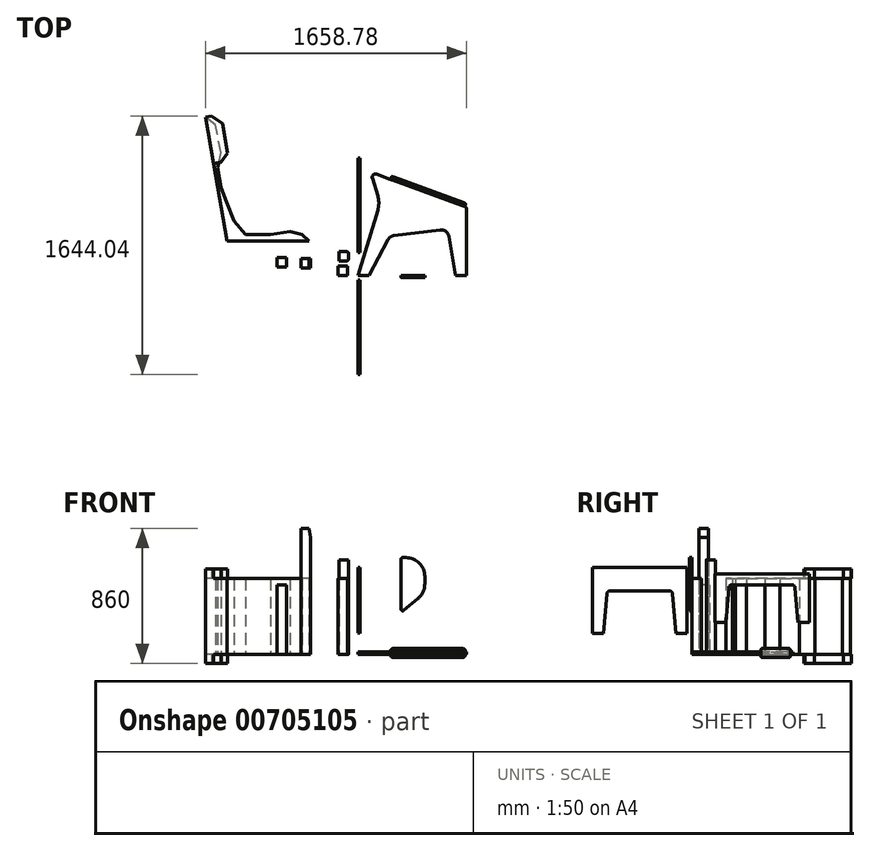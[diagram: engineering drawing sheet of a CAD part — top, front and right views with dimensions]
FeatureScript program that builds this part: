
annotation { "Feature Type Name" : "Feature", "Feature Type Description" : "" }
export const myFeature = defineFeature(function(context is Context, id is Id, definition is map)
    precondition{}
    {
        {
            var Q0;
            Q0=qCreatedBy(makeId("Top.planeOp"),FACE);
            var sketch = newSketch(context, id + "F0", { "sketchPlane" : qUnion([Q0])});
            skLineSegment(sketch, "E0.bottom", {"start": v(0, 0) * mm, "end": v(70, 0) * mm});
            skLineSegment(sketch, "E0.right", {"start": v(690, 0) * mm, "end": v(690, 420) * mm});
            skLineSegment(sketch, "E1", {"start": v(117.7, 642.3) * mm, "end": v(676.84, 438.8) * mm});
            skLineSegment(sketch, "E2", {"start": v(126.56, 503.75) * mm, "end": v(91.73, 617.66) * mm});
            skLineSegment(sketch, "E3", {"start": v(70, 0) * mm, "end": v(191.89, 227.17) * mm});
            skLineSegment(sketch, "E4", {"start": v(229.85, 253.16) * mm, "end": v(523.12, 289.17) * mm});
            skLineSegment(sketch, "E5", {"start": v(578.53, 247.8) * mm, "end": v(620, 0) * mm});
            skLineSegment(sketch, "E6", {"start": v(0, 0) * mm, "end": v(126.62, 416.24) * mm});
            skPoint(sketch, "E7.visualSharp", {"position": v(570.63, 295) * mm});
            skArc(sketch, "E7.filletArc", {"start": v(578.53, 247.8) * mm, "mid": v(559.13, 279.6) * mm, "end": v(523.12, 289.17) * mm});
            skPoint(sketch, "E8.visualSharp", {"position": v(204.13, 250) * mm});
            skArc(sketch, "E8.filletArc", {"start": v(229.85, 253.16) * mm, "mid": v(207.7, 244.79) * mm, "end": v(191.89, 227.17) * mm});
            skPoint(sketch, "E9.visualSharp", {"position": v(139.93, 460) * mm});
            skArc(sketch, "E9.filletArc", {"start": v(126.62, 416.24) * mm, "mid": v(133.11, 460) * mm, "end": v(126.56, 503.75) * mm});
            skArc(sketch, "E10.filletArc", {"start": v(690, 420) * mm, "mid": v(686.38, 431.47) * mm, "end": v(676.84, 438.8) * mm});
            skLineSegment(sketch, "E11.trimOffspring", {"start": v(620, 0) * mm, "end": v(690, 0) * mm});
            skPoint(sketch, "E12.visualSharp", {"position": v(80, 656.03) * mm});
            skArc(sketch, "E12.filletArc", {"start": v(117.7, 642.3) * mm, "mid": v(97.09, 638.02) * mm, "end": v(91.73, 617.66) * mm});
            skSolve(sketch);
        }
        {
            var Q0;
            Q0=makeQuery(id+"F0.imprint","IMPRINT",FACE,{"disambiguationData":[TD([[makeQuery(id+"F0.imprint","IMPRINT",EDGE,{"derivedFrom":sQuery(id+"F0.wireOp",EDGE,"E0.bottom")}),1.0]])]});
            extrude(context, id + "F1", {"entities" : qUnion([Q0]), "depth" : 15 * mm, "offsetDistance" : 25 * mm});
        }
        {
            var Q0;
            Q0=makeQuery(id+"F1.opExtrude","SWEPT_FACE",FACE,{"disambiguationData":[OSD([sQuery(id+"F0.wireOp",EDGE,"E1")])]});
            var sketch = newSketch(context, id + "F2", { "sketchPlane" : qUnion([Q0])});
            skLineSegment(sketch, "E13.bottom", {"start": v(-470.95, 35) * mm, "end": v(-0.95, 35) * mm});
            skLineSegment(sketch, "E13.top", {"start": v(-470.95, -20) * mm, "end": v(-0.95, -20) * mm});
            skLineSegment(sketch, "E13.left", {"start": v(-485.95, 20) * mm, "end": v(-485.95, -5) * mm});
            skLineSegment(sketch, "E13.right", {"start": v(14.05, 20) * mm, "end": v(14.05, -5) * mm});
            skPoint(sketch, "E14.visualSharp", {"position": v(-485.95, 35) * mm});
            skArc(sketch, "E14.filletArc", {"start": v(-470.95, 35) * mm, "mid": v(-481.55, 30.6) * mm, "end": v(-485.95, 20) * mm});
            skPoint(sketch, "E15.visualSharp", {"position": v(-485.95, -20) * mm});
            skArc(sketch, "E15.filletArc", {"start": v(-485.95, -5) * mm, "mid": v(-481.55, -15.6) * mm, "end": v(-470.95, -20) * mm});
            skPoint(sketch, "E16.visualSharp", {"position": v(14.05, 35) * mm});
            skArc(sketch, "E16.filletArc", {"start": v(14.05, 20) * mm, "mid": v(9.66, 30.6) * mm, "end": v(-0.95, 35) * mm});
            skPoint(sketch, "E17.visualSharp", {"position": v(14.05, -20) * mm});
            skArc(sketch, "E17.filletArc", {"start": v(-0.95, -20) * mm, "mid": v(9.66, -15.6) * mm, "end": v(14.05, -5) * mm});
            skSolve(sketch);
        }
        {
            var Q0;
            Q0 = qSketchRegion(id + "F2", true);
            extrude(context, id + "F3", {"entities" : qUnion([Q0]), "operationType" : NewBodyOperationType.ADD, "depth" : 20 * mm, "offsetDistance" : 25 * mm});
        }
        {
            var Q0;
            Q0=makeQuery(id+"F3.opExtrude","CAP_EDGE",EDGE,{"disambiguationData":[OSD([sQuery(id+"F2.wireOp",EDGE,"E13.top")])],"isStart":false});
            fillet(context, id + "F4", {"entities" : qUnion([Q0]), "radius" : 5 * mm, "tangentPropagation" : true, "allowEdgeOverflow" : false});
        }
        {
            var Q0;
            Q0=qCreatedBy(makeId("Front.planeOp"),FACE);
            var sketch = newSketch(context, id + "F5", { "sketchPlane" : qUnion([Q0])});
            skLineSegment(sketch, "E18.top", {"start": v(0, -1013.8) * mm, "end": v(626.68, -1013.8) * mm});
            skLineSegment(sketch, "E18.left", {"start": v(-123.43, -313.8) * mm, "end": v(0, -1013.8) * mm});
            skLineSegment(sketch, "E18.right", {"start": v(640.31, -922.17) * mm, "end": v(651.3, -984.47) * mm});
            skLineSegment(sketch, "E19", {"start": v(538.32, -839.6) * mm, "end": v(134.26, -853.8) * mm});
            skPoint(sketch, "E20.visualSharp", {"position": v(625.21, -836.54) * mm});
            skArc(sketch, "E20.filletArc", {"start": v(640.31, -922.17) * mm, "mid": v(604.75, -861.81) * mm, "end": v(538.32, -839.6) * mm});
            skPoint(sketch, "E21.visualSharp", {"position": v(656.47, -1013.8) * mm});
            skArc(sketch, "E21.filletArc", {"start": v(626.68, -1013.8) * mm, "mid": v(645.83, -1004.88) * mm, "end": v(651.3, -984.47) * mm});
            skLineSegment(sketch, "E22", {"start": v(39.04, -313.8) * mm, "end": v(134.26, -853.8) * mm});
            skLineSegment(sketch, "E23.top", {"start": v(-123.43, -13.8) * mm, "end": v(39.04, -13.8) * mm});
            skLineSegment(sketch, "E23.left", {"start": v(-123.43, -313.8) * mm, "end": v(-123.43, -13.8) * mm});
            skLineSegment(sketch, "E23.right", {"start": v(39.04, -313.8) * mm, "end": v(39.04, -13.8) * mm});
            skPoint(sketch, "E24.visualSharp", {"position": v(39.04, -13.8) * mm});
            skSolve(sketch);
        }
        {
            var Q0;
            Q0 = qSketchRegion(id + "F5", true);
            extrude(context, id + "F6", {"entities" : qUnion([Q0]), "depth" : 600 * mm, "offsetDistance" : 25 * mm});
        }
        {
            var Q0;
            Q0=makeQuery(id+"F6.opExtrude","SWEPT_EDGE",EDGE,{"disambiguationData":[OSD([sQuery(id+"F5.wireOp",EDGE,"E18.top"),sQuery(id+"F5.wireOp",EDGE,"E18.left")])]});
            fillet(context, id + "F7", {"entities" : qUnion([Q0]), "radius" : 50 * mm, "tangentPropagation" : true, "allowEdgeOverflow" : false});
        }
        {
            var Q0;
            Q0=makeQuery(id+"F6.opExtrude","SWEPT_FACE",FACE,{"disambiguationData":[OSD([sQuery(id+"F5.wireOp",EDGE,"E23.top")])]});
            var sketch = newSketch(context, id + "F8", { "sketchPlane" : qUnion([Q0])});
            skLineSegment(sketch, "E25", {"start": v(39.04, -600) * mm, "end": v(-123.43, -600) * mm});
            skLineSegment(sketch, "E26", {"start": v(-123.43, -600) * mm, "end": v(66.57, -689.38) * mm});
            skLineSegment(sketch, "E27", {"start": v(66.57, -689.38) * mm, "end": v(176, -689.38) * mm});
            skLineSegment(sketch, "E28", {"start": v(176, -689.38) * mm, "end": v(39.04, -600) * mm});
            skLineSegment(sketch, "E29", {"start": v(-123.43, -300) * mm, "end": v(-54.44, -300) * mm});
            skLineSegment(sketch, "E30.MirrorCS", {"start": v(-123.43, 0) * mm, "end": v(66.57, 89.38) * mm});
            skLineSegment(sketch, "E31.MirrorCS", {"start": v(39.04, 0) * mm, "end": v(-123.43, 0) * mm});
            skLineSegment(sketch, "E32.MirrorCS", {"start": v(176, 89.38) * mm, "end": v(39.04, 0) * mm});
            skLineSegment(sketch, "E33.MirrorCS", {"start": v(66.57, 89.38) * mm, "end": v(176, 89.38) * mm});
            skSolve(sketch);
        }
        {
            var Q0;
            Q0=makeQuery(id+"F8.imprint","IMPRINT",FACE,{"disambiguationData":[TD([[makeQuery(id+"F8.imprint","IMPRINT",EDGE,{"derivedFrom":sQuery(id+"F8.wireOp",EDGE,"E30.MirrorCS")}),-1.0]])]});
            var Q1;
            Q1=makeQuery(id+"F8.imprint","IMPRINT",FACE,{"disambiguationData":[TD([[makeQuery(id+"F8.imprint","IMPRINT",EDGE,{"derivedFrom":sQuery(id+"F8.wireOp",EDGE,"E25")}),-1.0]])]});
            extrude(context, id + "F9", {"entities" : qUnion([Q0, Q1]), "operationType" : NewBodyOperationType.ADD, "oppositeDirection" : true, "depth" : 300 * mm, "offsetDistance" : 25 * mm});
        }
        {
            var Q0;
            Q0=makeQuery(id+"F9.opExtrude","SWEPT_EDGE",EDGE,{"disambiguationData":[OSD([sQuery(id+"F8.wireOp",EDGE,"E27"),sQuery(id+"F8.wireOp",EDGE,"E28")])]});
            var Q1;
            Q1=makeQuery(id+"F9.opExtrude","SWEPT_EDGE",EDGE,{"disambiguationData":[OSD([sQuery(id+"F8.wireOp",EDGE,"E32.MirrorCS"),sQuery(id+"F8.wireOp",EDGE,"E33.MirrorCS")])]});
            var Q2;
            Q2=makeQuery(id+"F9.opExtrude","SWEPT_EDGE",EDGE,{"disambiguationData":[OSD([sQuery(id+"F8.wireOp",EDGE,"E26"),sQuery(id+"F8.wireOp",EDGE,"E27")])]});
            var Q3;
            {var subQ0=sQuery(id+"F5.wireOp",EDGE,"E23.left");Q3=makeQuery(id+"F9.boolean.opBoolean","MERGE",EDGE,{"derivedFrom":[makeQuery(id+"F6.opExtrude","CAP_EDGE",EDGE,{"disambiguationData":[OSD([subQ0])],"isStart":false}),makeQuery(id+"F9.opExtrude","SWEPT_EDGE",EDGE,{"disambiguationData":[OSD([sQuery(id+"F5.wireOp",EDGE,"E23.top"),subQ0,sQuery(id+"F8.wireOp",EDGE,"E25"),sQuery(id+"F8.wireOp",EDGE,"E26")])]})]});}
            var Q4;
            Q4=makeQuery(id+"F9.opExtrude","SWEPT_EDGE",EDGE,{"disambiguationData":[OSD([sQuery(id+"F8.wireOp",EDGE,"E30.MirrorCS"),sQuery(id+"F8.wireOp",EDGE,"E33.MirrorCS")])]});
            var Q5;
            {var subQ0=sQuery(id+"F5.wireOp",EDGE,"E23.left");Q5=makeQuery(id+"F9.boolean.opBoolean","MERGE",EDGE,{"derivedFrom":[makeQuery(id+"F6.opExtrude","CAP_EDGE",EDGE,{"disambiguationData":[OSD([subQ0])],"isStart":true}),makeQuery(id+"F9.opExtrude","SWEPT_EDGE",EDGE,{"disambiguationData":[OSD([sQuery(id+"F5.wireOp",EDGE,"E23.top"),subQ0,sQuery(id+"F8.wireOp",EDGE,"E30.MirrorCS"),sQuery(id+"F8.wireOp",EDGE,"E31.MirrorCS")])]})]});}
            var Q6;
            {var subQ0=sQuery(id+"F5.wireOp",EDGE,"E23.right");Q6=makeQuery(id+"F9.boolean.opBoolean","MERGE",EDGE,{"derivedFrom":[makeQuery(id+"F6.opExtrude","CAP_EDGE",EDGE,{"disambiguationData":[OSD([subQ0])],"isStart":false}),makeQuery(id+"F9.opExtrude","SWEPT_EDGE",EDGE,{"disambiguationData":[OSD([sQuery(id+"F5.wireOp",EDGE,"E23.top"),subQ0,sQuery(id+"F8.wireOp",EDGE,"E25"),sQuery(id+"F8.wireOp",EDGE,"E28")])]})]});}
            var Q7;
            {var subQ0=sQuery(id+"F5.wireOp",EDGE,"E23.right");Q7=makeQuery(id+"F9.boolean.opBoolean","MERGE",EDGE,{"derivedFrom":[makeQuery(id+"F6.opExtrude","CAP_EDGE",EDGE,{"disambiguationData":[OSD([subQ0])],"isStart":true}),makeQuery(id+"F9.opExtrude","SWEPT_EDGE",EDGE,{"disambiguationData":[OSD([sQuery(id+"F5.wireOp",EDGE,"E23.top"),subQ0,sQuery(id+"F8.wireOp",EDGE,"E31.MirrorCS"),sQuery(id+"F8.wireOp",EDGE,"E32.MirrorCS")])]})]});}
            fillet(context, id + "F10", {"entities" : qUnion([Q0, Q1, Q2, Q3, Q4, Q5, Q6, Q7]), "radius" : 10 * mm, "tangentPropagation" : true, "allowEdgeOverflow" : false});
        }
        {
            var Q0;
            Q0=qCreatedBy(makeId("Right.planeOp"),FACE);
            var sketch = newSketch(context, id + "F11", { "sketchPlane" : qUnion([Q0])});
            skLineSegment(sketch, "E34.bottom", {"start": v(-630.89, 552.12) * mm, "end": v(-30.89, 552.12) * mm});
            skLineSegment(sketch, "E34.top", {"start": v(-630.89, 132.12) * mm, "end": v(-560.89, 132.12) * mm});
            skLineSegment(sketch, "E34.left", {"start": v(-630.89, 552.12) * mm, "end": v(-630.89, 132.12) * mm});
            skLineSegment(sketch, "E34.right", {"start": v(-30.89, 552.12) * mm, "end": v(-30.89, 132.12) * mm});
            skLineSegment(sketch, "E35.bottom", {"start": v(145.52, 510.33) * mm, "end": v(745.52, 510.33) * mm});
            skLineSegment(sketch, "E35.top", {"start": v(145.52, 200.33) * mm, "end": v(215.52, 200.33) * mm});
            skLineSegment(sketch, "E35.left", {"start": v(145.52, 510.33) * mm, "end": v(145.52, 200.33) * mm});
            skLineSegment(sketch, "E35.right", {"start": v(745.52, 510.33) * mm, "end": v(745.52, 200.33) * mm});
            skLineSegment(sketch, "E36", {"start": v(-560.89, 132.12) * mm, "end": v(-538.86, 383.87) * mm});
            skLineSegment(sketch, "E37", {"start": v(-518.94, 402.12) * mm, "end": v(-142.83, 402.12) * mm});
            skLineSegment(sketch, "E38", {"start": v(-122.91, 383.87) * mm, "end": v(-100.89, 132.12) * mm});
            skLineSegment(sketch, "E39", {"start": v(215.52, 200.33) * mm, "end": v(234.92, 422.07) * mm});
            skLineSegment(sketch, "E40", {"start": v(254.85, 440.33) * mm, "end": v(636.2, 440.33) * mm});
            skLineSegment(sketch, "E41", {"start": v(656.12, 422.07) * mm, "end": v(675.52, 200.33) * mm});
            skLineSegment(sketch, "E42.trimOffspring", {"start": v(675.52, 200.33) * mm, "end": v(745.52, 200.33) * mm});
            skPoint(sketch, "E43.visualSharp", {"position": v(236.52, 440.33) * mm});
            skArc(sketch, "E43.filletArc", {"start": v(254.85, 440.33) * mm, "mid": v(241.34, 435.07) * mm, "end": v(234.92, 422.07) * mm});
            skPoint(sketch, "E44.visualSharp", {"position": v(654.53, 440.33) * mm});
            skArc(sketch, "E44.filletArc", {"start": v(656.12, 422.07) * mm, "mid": v(649.71, 435.07) * mm, "end": v(636.2, 440.33) * mm});
            skLineSegment(sketch, "E45.trimOffspring", {"start": v(-100.89, 132.12) * mm, "end": v(-30.89, 132.12) * mm});
            skPoint(sketch, "E46.visualSharp", {"position": v(-537.26, 402.12) * mm});
            skArc(sketch, "E46.filletArc", {"start": v(-518.94, 402.12) * mm, "mid": v(-532.45, 396.87) * mm, "end": v(-538.86, 383.87) * mm});
            skPoint(sketch, "E47.visualSharp", {"position": v(-124.5, 402.12) * mm});
            skArc(sketch, "E47.filletArc", {"start": v(-122.91, 383.87) * mm, "mid": v(-129.32, 396.87) * mm, "end": v(-142.83, 402.12) * mm});
            skSolve(sketch);
        }
        {
            var Q0;
            Q0=makeQuery(id+"F11.imprint","IMPRINT",FACE,{"disambiguationData":[TD([[makeQuery(id+"F11.imprint","IMPRINT",EDGE,{"derivedFrom":sQuery(id+"F11.wireOp",EDGE,"E34.bottom")}),-1.0]])]});
            var Q1;
            Q1=makeQuery(id+"F11.imprint","IMPRINT",FACE,{"disambiguationData":[TD([[makeQuery(id+"F11.imprint","IMPRINT",EDGE,{"derivedFrom":sQuery(id+"F11.wireOp",EDGE,"E35.bottom")}),-1.0]])]});
            extrude(context, id + "F12", {"entities" : qUnion([Q0, Q1]), "depth" : 15 * mm, "offsetDistance" : 25 * mm});
        }
        {
            var Q0;
            Q0=makeQuery(id+"F12.opExtrude","CAP_EDGE",EDGE,{"disambiguationData":[OSD([sQuery(id+"F11.wireOp",EDGE,"E34.top")])],"isStart":true});
            var Q1;
            Q1=makeQuery(id+"F12.opExtrude","CAP_EDGE",EDGE,{"disambiguationData":[OSD([sQuery(id+"F11.wireOp",EDGE,"E45.trimOffspring")])],"isStart":true});
            chamfer(context, id + "F13", {"entities" : qUnion([Q0, Q1]), "chamferType" : ChamferType.OFFSET_ANGLE, "width" : 15 * mm, "oppositeDirection" : false, "angle" : 15 * degree, "tangentPropagation" : true});
        }
        {
            var Q0;
            Q0=makeQuery(id+"F6.opExtrude","SWEPT_BODY",BODY,{"disambiguationData":[OSD([sQuery(id+"F5.wireOp",EDGE,"E18.top"),sQuery(id+"F5.wireOp",EDGE,"E18.left"),sQuery(id+"F5.wireOp",EDGE,"E18.right"),sQuery(id+"F5.wireOp",EDGE,"E19"),sQuery(id+"F5.wireOp",EDGE,"E20.filletArc"),sQuery(id+"F5.wireOp",EDGE,"E21.filletArc"),sQuery(id+"F5.wireOp",EDGE,"E22"),sQuery(id+"F5.wireOp",EDGE,"E23.top"),sQuery(id+"F5.wireOp",EDGE,"E23.left"),sQuery(id+"F5.wireOp",EDGE,"E23.right")])]});
            deleteBodies(context, id + "F14", {"entities" : qUnion([Q0])});
        }
        {
            var Q0;
            Q0=qCreatedBy(makeId("Top.planeOp"),FACE);
            var sketch = newSketch(context, id + "F15", { "sketchPlane" : qUnion([Q0])});
            skLineSegment(sketch, "E48.bottom", {"start": v(-511.95, 112.3) * mm, "end": v(-451.95, 112.3) * mm});
            skLineSegment(sketch, "E48.top", {"start": v(-511.95, 52.3) * mm, "end": v(-451.95, 52.3) * mm});
            skLineSegment(sketch, "E48.left", {"start": v(-511.95, 112.3) * mm, "end": v(-511.95, 52.3) * mm});
            skLineSegment(sketch, "E48.right", {"start": v(-451.95, 112.3) * mm, "end": v(-451.95, 52.3) * mm});
            skSolve(sketch);
        }
        {
            var Q0;
            Q0=makeQuery(id+"F15.imprint","IMPRINT",FACE,{"disambiguationData":[TD([[makeQuery(id+"F15.imprint","IMPRINT",EDGE,{"derivedFrom":sQuery(id+"F15.wireOp",EDGE,"E48.bottom")}),-1.0]])]});
            extrude(context, id + "F16", {"entities" : qUnion([Q0]), "depth" : 440 * mm, "offsetDistance" : 25 * mm});
        }
        {
            var Q0;
            Q0=qCreatedBy(makeId("Top.planeOp"),FACE);
            var sketch = newSketch(context, id + "F17", { "sketchPlane" : qUnion([Q0])});
            skLineSegment(sketch, "E49.bottom", {"start": v(-360.7, 105.75) * mm, "end": v(-300.7, 105.75) * mm});
            skLineSegment(sketch, "E49.top", {"start": v(-360.7, 45.75) * mm, "end": v(-300.7, 45.75) * mm});
            skLineSegment(sketch, "E49.left", {"start": v(-360.7, 105.75) * mm, "end": v(-360.7, 45.75) * mm});
            skLineSegment(sketch, "E49.right", {"start": v(-300.7, 105.75) * mm, "end": v(-300.7, 45.75) * mm});
            skSolve(sketch);
        }
        {
            var Q0;
            Q0=makeQuery(id+"F17.imprint","IMPRINT",FACE,{"disambiguationData":[TD([[makeQuery(id+"F17.imprint","IMPRINT",EDGE,{"derivedFrom":sQuery(id+"F17.wireOp",EDGE,"E49.bottom")}),-1.0]])]});
            extrude(context, id + "F18", {"entities" : qUnion([Q0]), "depth" : 800 * mm, "offsetDistance" : 25 * mm});
        }
        {
            var Q0;
            Q0=makeQuery(id+"F18.opExtrude","CAP_EDGE",EDGE,{"disambiguationData":[OSD([sQuery(id+"F17.wireOp",EDGE,"E49.right")])],"isStart":false});
            chamfer(context, id + "F19", {"entities" : qUnion([Q0]), "chamferType" : ChamferType.OFFSET_ANGLE, "width" : 60 * mm, "oppositeDirection" : false, "angle" : 10 * degree, "tangentPropagation" : true});
        }
        {
            var Q0;
            Q0=qCreatedBy(makeId("Top.planeOp"),FACE);
            var sketch = newSketch(context, id + "F20", { "sketchPlane" : qUnion([Q0])});
            skLineSegment(sketch, "E50.bottom", {"start": v(-59.06, 91.57) * mm, "end": v(-119.06, 91.57) * mm});
            skLineSegment(sketch, "E50.top", {"start": v(-59.06, 151.57) * mm, "end": v(-119.06, 151.57) * mm});
            skLineSegment(sketch, "E50.left", {"start": v(-59.06, 91.57) * mm, "end": v(-59.06, 151.57) * mm});
            skLineSegment(sketch, "E50.right", {"start": v(-119.06, 91.57) * mm, "end": v(-119.06, 151.57) * mm});
            skSolve(sketch);
        }
        {
            var Q0;
            Q0=makeQuery(id+"F20.imprint","IMPRINT",FACE,{"disambiguationData":[TD([[makeQuery(id+"F20.imprint","IMPRINT",EDGE,{"derivedFrom":sQuery(id+"F20.wireOp",EDGE,"E50.bottom")}),-1.0]])]});
            extrude(context, id + "F21", {"entities" : qUnion([Q0]), "depth" : 600 * mm, "offsetDistance" : 25 * mm});
        }
        {
            var Q0;
            Q0=qCreatedBy(makeId("Front.planeOp"),FACE);
            var sketch = newSketch(context, id + "F22", { "sketchPlane" : qUnion([Q0])});
            skLineSegment(sketch, "E51.bottom", {"start": v(284.77, 613.26) * mm, "end": v(304.77, 613.26) * mm});
            skLineSegment(sketch, "E51.left", {"start": v(274.77, 603.26) * mm, "end": v(274.77, 284.7) * mm});
            skLineSegment(sketch, "E51.right", {"start": v(424.77, 493.26) * mm, "end": v(424.77, 445.08) * mm});
            skLineSegment(sketch, "E52", {"start": v(291.2, 277.04) * mm, "end": v(381.9, 353.15) * mm});
            skPoint(sketch, "E53.visualSharp", {"position": v(424.77, 613.26) * mm});
            skArc(sketch, "E53.filletArc", {"start": v(424.77, 493.26) * mm, "mid": v(389.63, 578.11) * mm, "end": v(304.77, 613.26) * mm});
            skPoint(sketch, "E54.visualSharp", {"position": v(424.77, 389.12) * mm});
            skArc(sketch, "E54.filletArc", {"start": v(381.9, 353.15) * mm, "mid": v(413.53, 394.37) * mm, "end": v(424.77, 445.08) * mm});
            skPoint(sketch, "E55.visualSharp", {"position": v(274.77, 263.26) * mm});
            skArc(sketch, "E55.filletArc", {"start": v(274.77, 284.7) * mm, "mid": v(280.55, 275.64) * mm, "end": v(291.2, 277.04) * mm});
            skPoint(sketch, "E56.visualSharp", {"position": v(274.77, 613.26) * mm});
            skArc(sketch, "E56.filletArc", {"start": v(284.77, 613.26) * mm, "mid": v(277.7, 610.33) * mm, "end": v(274.77, 603.26) * mm});
            skSolve(sketch);
        }
        {
            var Q0;
            Q0=makeQuery(id+"F22.imprint","IMPRINT",FACE,{"disambiguationData":[TD([[makeQuery(id+"F22.imprint","IMPRINT",EDGE,{"derivedFrom":sQuery(id+"F22.wireOp",EDGE,"E51.bottom")}),-1.0]])]});
            extrude(context, id + "F23", {"entities" : qUnion([Q0]), "depth" : 15 * mm, "offsetDistance" : 25 * mm});
        }
        {
            var Q0;
            Q0=makeQuery(id+"F21.opExtrude","SWEPT_EDGE",EDGE,{"disambiguationData":[OSD([sQuery(id+"F20.wireOp",EDGE,"E50.top"),sQuery(id+"F20.wireOp",EDGE,"E50.left")])]});
            var Q1;
            Q1=makeQuery(id+"F21.opExtrude","SWEPT_EDGE",EDGE,{"disambiguationData":[OSD([sQuery(id+"F20.wireOp",EDGE,"E50.bottom"),sQuery(id+"F20.wireOp",EDGE,"E50.left")])]});
            fillet(context, id + "F24", {"entities" : qUnion([Q0, Q1]), "radius" : 15 * mm, "tangentPropagation" : true, "allowEdgeOverflow" : false});
        }
        {
            var Q0;
            Q0=qCreatedBy(makeId("Top.planeOp"),FACE);
            var sketch = newSketch(context, id + "F25", { "sketchPlane" : qUnion([Q0])});
            skLineSegment(sketch, "E57.bottom", {"start": v(-125.9, 60) * mm, "end": v(-65.9, 60) * mm});
            skLineSegment(sketch, "E57.top", {"start": v(-125.9, 0) * mm, "end": v(-65.9, 0) * mm});
            skLineSegment(sketch, "E57.left", {"start": v(-125.9, 60) * mm, "end": v(-125.9, 0) * mm});
            skLineSegment(sketch, "E57.right", {"start": v(-65.9, 60) * mm, "end": v(-65.9, 0) * mm});
            skSolve(sketch);
        }
        {
            var Q0;
            Q0=makeQuery(id+"F25.imprint","IMPRINT",FACE,{"disambiguationData":[TD([[makeQuery(id+"F25.imprint","IMPRINT",EDGE,{"derivedFrom":sQuery(id+"F25.wireOp",EDGE,"E57.bottom")}),-1.0]])]});
            extrude(context, id + "F26", {"entities" : qUnion([Q0]), "depth" : 480 * mm, "offsetDistance" : 25 * mm});
        }
        {
            var Q0;
            Q0=qCreatedBy(makeId("Top.planeOp"),FACE);
            var sketch = newSketch(context, id + "F27", { "sketchPlane" : qUnion([Q0])});
            skLineSegment(sketch, "E58.bottom", {"start": v(-309.86, 218.35) * mm, "end": v(-829.86, 218.35) * mm});
            skLineSegment(sketch, "E59", {"start": v(-968.78, 1006.2) * mm, "end": v(-829.86, 218.35) * mm});
            skLineSegment(sketch, "E60", {"start": v(-309.86, 218.35) * mm, "end": v(-353.8, 259.62) * mm});
            skLineSegment(sketch, "E61", {"start": v(-353.8, 259.62) * mm, "end": v(-431.44, 277.12) * mm});
            skLineSegment(sketch, "E62", {"start": v(-431.44, 277.12) * mm, "end": v(-553.32, 259.62) * mm});
            skLineSegment(sketch, "E63", {"start": v(-553.32, 259.62) * mm, "end": v(-711.8, 259.01) * mm});
            skLineSegment(sketch, "E64", {"start": v(-711.8, 259.01) * mm, "end": v(-785.68, 346.5) * mm});
            skLineSegment(sketch, "E65", {"start": v(-785.68, 346.5) * mm, "end": v(-833.32, 464.42) * mm});
            skLineSegment(sketch, "E66", {"start": v(-833.32, 464.42) * mm, "end": v(-868.17, 558.7) * mm});
            skLineSegment(sketch, "E67", {"start": v(-868.17, 558.7) * mm, "end": v(-890.23, 683.8) * mm});
            skLineSegment(sketch, "E68", {"start": v(-890.23, 683.8) * mm, "end": v(-868.17, 780.85) * mm});
            skLineSegment(sketch, "E69", {"start": v(-868.17, 780.85) * mm, "end": v(-904.69, 956.22) * mm});
            skLineSegment(sketch, "E70", {"start": v(-904.69, 956.22) * mm, "end": v(-968.78, 1006.2) * mm});
            skSolve(sketch);
        }
        {
            var Q0;
            Q0=makeQuery(id+"F27.imprint","IMPRINT",FACE,{"disambiguationData":[TD([[makeQuery(id+"F27.imprint","IMPRINT",EDGE,{"derivedFrom":sQuery(id+"F27.wireOp",EDGE,"E58.bottom")}),-1.0]])]});
            extrude(context, id + "F28", {"entities" : qUnion([Q0]), "depth" : 480 * mm, "offsetDistance" : 25 * mm});
        }
        {
            var Q0;
            Q0=makeQuery(id+"F28.opExtrude","SWEPT_FACE",FACE,{"disambiguationData":[OSD([sQuery(id+"F27.wireOp",EDGE,"E59")])]});
            var sketch = newSketch(context, id + "F29", { "sketchPlane" : qUnion([Q0])});
            skLineSegment(sketch, "E71.bottom", {"start": v(-1159.14, 480) * mm, "end": v(-859.14, 480) * mm});
            skLineSegment(sketch, "E71.top", {"start": v(-1159.14, 540) * mm, "end": v(-859.14, 540) * mm});
            skLineSegment(sketch, "E71.left", {"start": v(-1159.14, 480) * mm, "end": v(-1159.14, 540) * mm});
            skLineSegment(sketch, "E71.right", {"start": v(-859.14, 480) * mm, "end": v(-859.14, 540) * mm});
            skLineSegment(sketch, "E72.bottom", {"start": v(-1159.14, 0) * mm, "end": v(-859.14, 0) * mm});
            skLineSegment(sketch, "E72.top", {"start": v(-1159.14, -60) * mm, "end": v(-859.14, -60) * mm});
            skLineSegment(sketch, "E72.left", {"start": v(-1159.14, 0) * mm, "end": v(-1159.14, -60) * mm});
            skLineSegment(sketch, "E72.right", {"start": v(-859.14, 0) * mm, "end": v(-859.14, -60) * mm});
            skSolve(sketch);
        }
        {
            var Q0;
            Q0=makeQuery(id+"F29.imprint","IMPRINT",FACE,{"disambiguationData":[TD([[makeQuery(id+"F29.imprint","IMPRINT",EDGE,{"derivedFrom":sQuery(id+"F29.wireOp",EDGE,"E72.bottom")}),-1.0]])]});
            var Q1;
            Q1=makeQuery(id+"F29.imprint","IMPRINT",FACE,{"disambiguationData":[TD([[makeQuery(id+"F29.imprint","IMPRINT",EDGE,{"derivedFrom":sQuery(id+"F29.wireOp",EDGE,"E71.bottom")}),1.0]])]});
            extrude(context, id + "F30", {"entities" : qUnion([Q0, Q1]), "operationType" : NewBodyOperationType.ADD, "oppositeDirection" : true, "depth" : 100 * mm, "offsetDistance" : 25 * mm});
        }
        {
            var Q0;
            Q0=makeQuery(id+"F30.opExtrude","CAP_EDGE",EDGE,{"disambiguationData":[OSD([sQuery(id+"F29.wireOp",EDGE,"E71.right")])],"isStart":false});
            var Q1;
            Q1=makeQuery(id+"F30.opExtrude","CAP_EDGE",EDGE,{"disambiguationData":[OSD([sQuery(id+"F29.wireOp",EDGE,"E72.right")])],"isStart":false});
            chamfer(context, id + "F31", {"entities" : qUnion([Q0, Q1]), "width" : 50 * mm, "tangentPropagation" : true});
        }
        {
            var Q0;
            Q0=makeQuery(id+"F30.opExtrude","CAP_EDGE",EDGE,{"disambiguationData":[OSD([sQuery(id+"F29.wireOp",EDGE,"E71.left")])],"isStart":false});
            var Q1;
            Q1=makeQuery(id+"F30.opExtrude","CAP_EDGE",EDGE,{"disambiguationData":[OSD([sQuery(id+"F29.wireOp",EDGE,"E72.left")])],"isStart":false});
            chamfer(context, id + "F32", {"entities" : qUnion([Q0, Q1]), "width" : 60 * mm, "tangentPropagation" : true});
        }
    });
